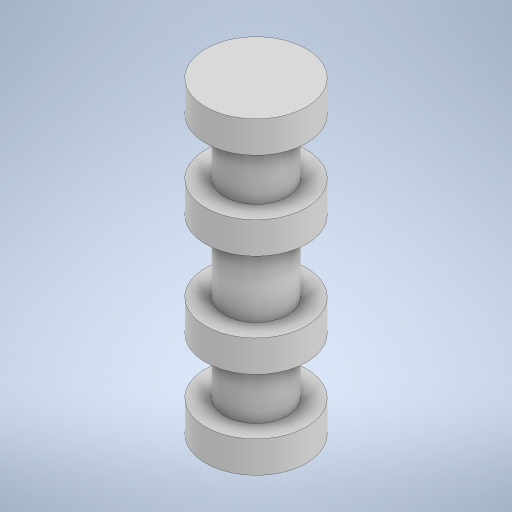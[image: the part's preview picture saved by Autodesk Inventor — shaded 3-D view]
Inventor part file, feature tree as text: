
AUTODESK INVENTOR PART (.ipt)
format: ipt  version: 2023 (Build 270158000, 158)  size: 272,384 bytes
history: native  units: in
note: dims shown in document units (in); Inventor stores cm internally (conversion verified against a paired STEP export)
features: revolve x1
ambient origin geometry x8: Origin, YZ Plane, XZ Plane, XY Plane, X Axis, Y Axis, Z Axis, Center Point
bodies: Solid1 (feature_tree)
feature tree (1):
  revolve  "Revolution1"  [1 undecoded]
note: 1 required parameter value undecoded (feature->parameter linkage not recoverable at this tier; creation-order binding heuristic only, values carry confidence <= 0.55)
